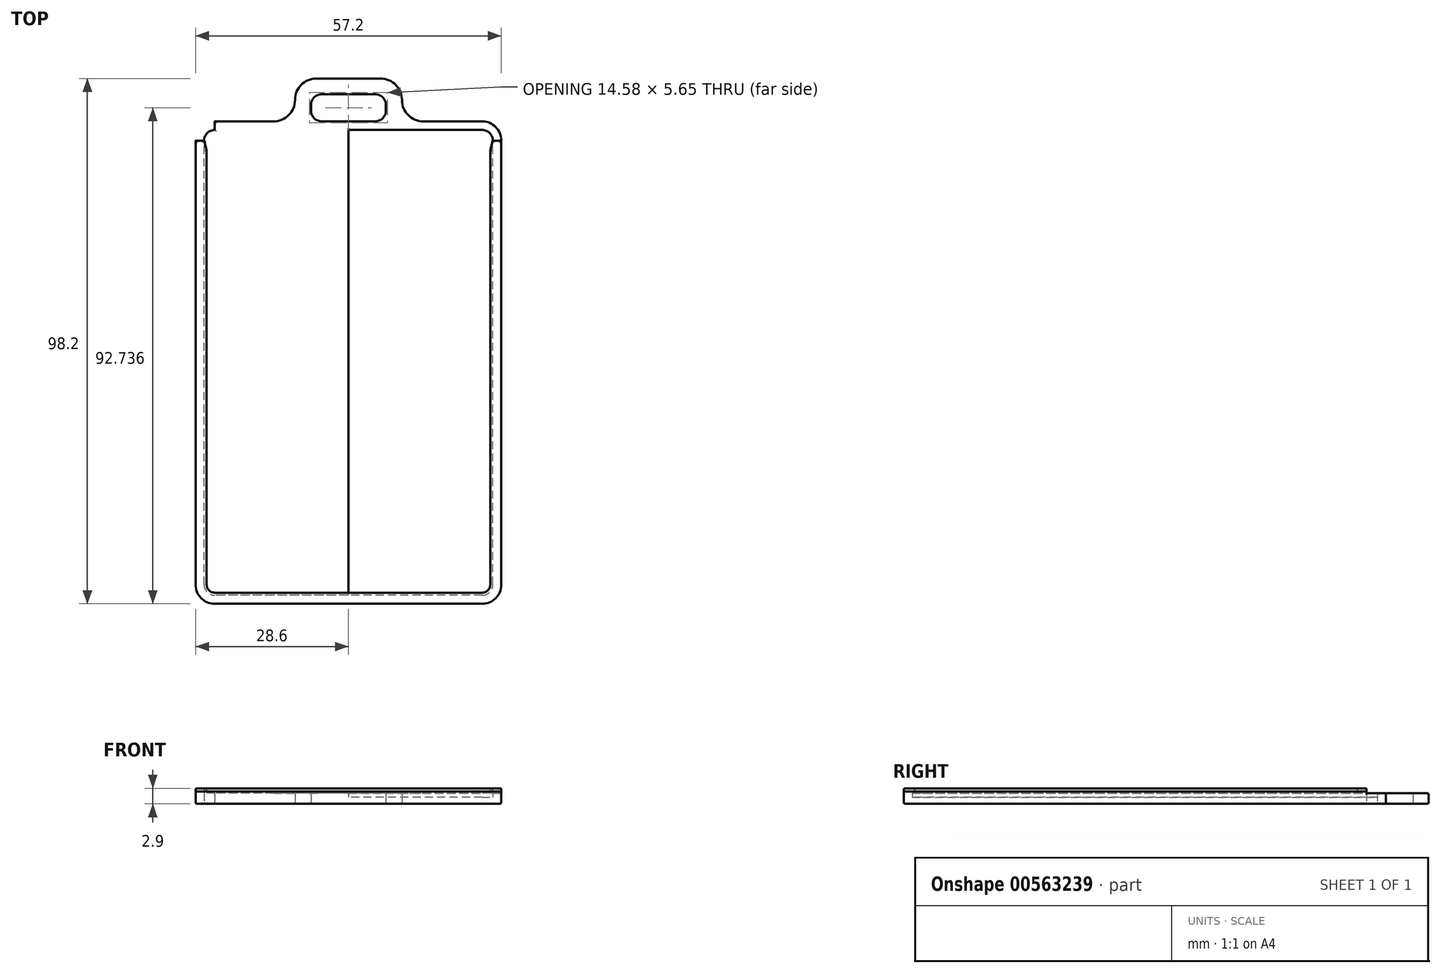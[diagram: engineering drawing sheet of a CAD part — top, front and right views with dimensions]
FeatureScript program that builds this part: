
annotation { "Feature Type Name" : "Feature", "Feature Type Description" : "" }
export const myFeature = defineFeature(function(context is Context, id is Id, definition is map)
    precondition{}
    {
        {
            var Q0;
            Q0=qCreatedBy(makeId("Top.planeOp"),FACE);
            var sketch = newSketch(context, id + "F0", { "sketchPlane" : qUnion([Q0])});
            skLineSegment(sketch, "E0.bottom", {"start": v(0, 0) * mm, "end": v(25, 0) * mm});
            skLineSegment(sketch, "E0.top", {"start": v(0, 87) * mm, "end": v(25, 87) * mm});
            skLineSegment(sketch, "E0.left", {"start": v(0, 0) * mm, "end": v(0, 87) * mm});
            skLineSegment(sketch, "E0.right", {"start": v(27, 2) * mm, "end": v(27, 85) * mm});
            skPoint(sketch, "E1.visualSharp", {"position": v(27, 87) * mm});
            skArc(sketch, "E1.filletArc", {"start": v(27, 85) * mm, "mid": v(26.41, 86.41) * mm, "end": v(25, 87) * mm});
            skPoint(sketch, "E2.visualSharp", {"position": v(27, 0) * mm});
            skArc(sketch, "E2.filletArc", {"start": v(25, 0) * mm, "mid": v(26.41, 0.59) * mm, "end": v(27, 2) * mm});
            skLineSegment(sketch, "E3.0", {"start": v(0, -1.6) * mm, "end": v(25, -1.6) * mm});
            skLineSegment(sketch, "E3.1", {"start": v(0, 88.6) * mm, "end": v(5, 88.6) * mm});
            skArc(sketch, "E3.2", {"start": v(28.6, 85) * mm, "mid": v(27.55, 87.55) * mm, "end": v(25, 88.6) * mm});
            skLineSegment(sketch, "E3.3", {"start": v(28.6, 2) * mm, "end": v(28.6, 85) * mm});
            skArc(sketch, "E3.4", {"start": v(25, -1.6) * mm, "mid": v(27.55, -0.55) * mm, "end": v(28.6, 2) * mm});
            skLineSegment(sketch, "E4", {"start": v(0, 88.6) * mm, "end": v(0, 87) * mm});
            skLineSegment(sketch, "E5", {"start": v(25, 88.6) * mm, "end": v(25, 87) * mm});
            skLineSegment(sketch, "E6", {"start": v(0, -1.6) * mm, "end": v(0, 0) * mm});
            skLineSegment(sketch, "E7", {"start": v(25, 0) * mm, "end": v(25, -1.6) * mm});
            skLineSegment(sketch, "E8", {"start": v(10, 92.6) * mm, "end": v(10, 92.6) * mm});
            skLineSegment(sketch, "E9", {"start": v(6, 96.6) * mm, "end": v(0, 96.6) * mm});
            skLineSegment(sketch, "E10", {"start": v(7, 90.6) * mm, "end": v(7, 91.67) * mm});
            skLineSegment(sketch, "E11", {"start": v(5, 93.67) * mm, "end": v(0, 93.67) * mm});
            skLineSegment(sketch, "E12", {"start": v(0, 93.67) * mm, "end": v(0, 96.6) * mm});
            skPoint(sketch, "E13.visualSharp", {"position": v(7, 93.67) * mm});
            skArc(sketch, "E13.filletArc", {"start": v(7, 91.67) * mm, "mid": v(6.41, 93.09) * mm, "end": v(5, 93.67) * mm});
            skPoint(sketch, "E14.visualSharp", {"position": v(10, 96.6) * mm});
            skArc(sketch, "E14.filletArc", {"start": v(10, 92.6) * mm, "mid": v(8.83, 95.43) * mm, "end": v(6, 96.6) * mm});
            skPoint(sketch, "E15.newPointB", {"position": v(7, 88.67) * mm});
            skArc(sketch, "E15.filletArc", {"start": v(5, 88.6) * mm, "mid": v(6.41, 89.19) * mm, "end": v(7, 90.6) * mm});
            skLineSegment(sketch, "E16", {"start": v(14, 88.6) * mm, "end": v(25, 88.6) * mm});
            skPoint(sketch, "E17.visualSharp", {"position": v(10, 88.6) * mm});
            skArc(sketch, "E17.filletArc", {"start": v(10, 92.6) * mm, "mid": v(11.17, 89.77) * mm, "end": v(14, 88.6) * mm});
            skLineSegment(sketch, "E18", {"start": v(0, 105.46) * mm, "end": v(0, -5) * mm, "construction": true});
            skLineSegment(sketch, "E19.MirrorCS", {"start": v(-6, 96.6) * mm, "end": v(0, 96.6) * mm});
            skLineSegment(sketch, "E20.MirrorCS", {"start": v(-5, 93.67) * mm, "end": v(0, 93.67) * mm});
            skArc(sketch, "E21.MirrorCS", {"start": v(-7, 91.67) * mm, "mid": v(-6.41, 93.09) * mm, "end": v(-5, 93.67) * mm});
            skLineSegment(sketch, "E22.MirrorCS", {"start": v(-7, 90.6) * mm, "end": v(-7, 91.67) * mm});
            skArc(sketch, "E23.MirrorCS", {"start": v(-5, 88.6) * mm, "mid": v(-6.41, 89.19) * mm, "end": v(-7, 90.6) * mm});
            skLineSegment(sketch, "E24.MirrorCS", {"start": v(0, 88.6) * mm, "end": v(-5, 88.6) * mm});
            skArc(sketch, "E25.MirrorCS", {"start": v(-10, 92.6) * mm, "mid": v(-8.83, 95.43) * mm, "end": v(-6, 96.6) * mm});
            skArc(sketch, "E26.MirrorCS", {"start": v(-10, 92.6) * mm, "mid": v(-11.17, 89.77) * mm, "end": v(-14, 88.6) * mm});
            skLineSegment(sketch, "E27.MirrorCS", {"start": v(0, 87) * mm, "end": v(-25, 87) * mm});
            skLineSegment(sketch, "E28.MirrorCS", {"start": v(-14, 88.6) * mm, "end": v(-25, 88.6) * mm});
            skArc(sketch, "E29.MirrorCS", {"start": v(-27, 85) * mm, "mid": v(-26.41, 86.41) * mm, "end": v(-25, 87) * mm});
            skArc(sketch, "E30.MirrorCS", {"start": v(-28.6, 85) * mm, "mid": v(-27.55, 87.55) * mm, "end": v(-25, 88.6) * mm});
            skLineSegment(sketch, "E31.MirrorCS", {"start": v(-28.6, 2) * mm, "end": v(-28.6, 85) * mm});
            skLineSegment(sketch, "E32.MirrorCS", {"start": v(-27, 2) * mm, "end": v(-27, 85) * mm});
            skArc(sketch, "E33.MirrorCS", {"start": v(-25, 0) * mm, "mid": v(-26.41, 0.59) * mm, "end": v(-27, 2) * mm});
            skArc(sketch, "E34.MirrorCS", {"start": v(-25, -1.6) * mm, "mid": v(-27.55, -0.55) * mm, "end": v(-28.6, 2) * mm});
            skLineSegment(sketch, "E35.MirrorCS", {"start": v(-25, 0) * mm, "end": v(-25, -1.6) * mm});
            skLineSegment(sketch, "E36.MirrorCS", {"start": v(0, 0) * mm, "end": v(-25, 0) * mm});
            skLineSegment(sketch, "E37.MirrorCS", {"start": v(0, -1.6) * mm, "end": v(-25, -1.6) * mm});
            skLineSegment(sketch, "E38.MirrorCS", {"start": v(-25, 88.6) * mm, "end": v(-25, 87) * mm});
            skLineSegment(sketch, "E39", {"start": v(-28.6, 85) * mm, "end": v(-27, 85) * mm});
            skLineSegment(sketch, "E40", {"start": v(27, 85) * mm, "end": v(28.6, 85) * mm});
            skPoint(sketch, "E41", {"position": v(0, 50.23) * mm});
            skSolve(sketch);
        }
        {
            var Q0;
            Q0=makeQuery(id+"F0.imprint","IMPRINT",FACE,{"disambiguationData":[TD([[makeQuery(id+"F0.imprint","IMPRINT",EDGE,{"derivedFrom":sQuery(id+"F0.wireOp",EDGE,"E0.left")}),1.0]])]});
            var Q1;
            Q1=makeQuery(id+"F0.imprint","IMPRINT",FACE,{"disambiguationData":[TD([[makeQuery(id+"F0.imprint","IMPRINT",EDGE,{"derivedFrom":sQuery(id+"F0.wireOp",EDGE,"E0.bottom")}),1.0]])]});
            extrude(context, id + "F1", {"entities" : qUnion([Q0, Q1]), "depth" : 1.2 * mm, "offsetDistance" : 25 * mm});
        }
        {
            var Q0;
            Q0=makeQuery(id+"F0.imprint","IMPRINT",FACE,{"disambiguationData":[TD([[makeQuery(id+"F0.imprint","IMPRINT",EDGE,{"derivedFrom":sQuery(id+"F0.wireOp",EDGE,"E0.right")}),-1.0]])]});
            var Q1;
            Q1=makeQuery(id+"F0.imprint","IMPRINT",FACE,{"disambiguationData":[TD([[makeQuery(id+"F0.imprint","IMPRINT",EDGE,{"derivedFrom":sQuery(id+"F0.wireOp",EDGE,"E6")}),1.0]])]});
            var Q2;
            Q2=makeQuery(id+"F0.imprint","IMPRINT",FACE,{"disambiguationData":[TD([[makeQuery(id+"F0.imprint","IMPRINT",EDGE,{"derivedFrom":sQuery(id+"F0.wireOp",EDGE,"E0.bottom")}),-1.0]])]});
            var Q3;
            Q3=makeQuery(id+"F0.imprint","IMPRINT",FACE,{"disambiguationData":[TD([[makeQuery(id+"F0.imprint","IMPRINT",EDGE,{"derivedFrom":sQuery(id+"F0.wireOp",EDGE,"E31.MirrorCS")}),-1.0]])]});
            extrude(context, id + "F2", {"entities" : qUnion([Q0, Q1, Q2, Q3]), "operationType" : NewBodyOperationType.ADD, "depth" : 2.3 * mm, "offsetDistance" : 25 * mm});
        }
        {
            var Q0;
            Q0=makeQuery(id+"F2.opExtrude","CAP_FACE",FACE,{"disambiguationData":[OSD([sQuery(id+"F0.wireOp",EDGE,"E0.bottom"),sQuery(id+"F0.wireOp",EDGE,"E0.top"),sQuery(id+"F0.wireOp",EDGE,"E0.right"),sQuery(id+"F0.wireOp",EDGE,"E1.filletArc"),sQuery(id+"F0.wireOp",EDGE,"E2.filletArc"),sQuery(id+"F0.wireOp",EDGE,"E3.0"),sQuery(id+"F0.wireOp",EDGE,"E3.1"),sQuery(id+"F0.wireOp",EDGE,"E3.2"),sQuery(id+"F0.wireOp",EDGE,"E3.3"),sQuery(id+"F0.wireOp",EDGE,"E3.4"),sQuery(id+"F0.wireOp",EDGE,"E9"),sQuery(id+"F0.wireOp",EDGE,"E10"),sQuery(id+"F0.wireOp",EDGE,"E11"),sQuery(id+"F0.wireOp",EDGE,"E13.filletArc"),sQuery(id+"F0.wireOp",EDGE,"E14.filletArc"),sQuery(id+"F0.wireOp",EDGE,"E15.filletArc"),sQuery(id+"F0.wireOp",EDGE,"E16"),sQuery(id+"F0.wireOp",EDGE,"E17.filletArc"),sQuery(id+"F0.wireOp",EDGE,"E19.MirrorCS"),sQuery(id+"F0.wireOp",EDGE,"E20.MirrorCS"),sQuery(id+"F0.wireOp",EDGE,"E21.MirrorCS"),sQuery(id+"F0.wireOp",EDGE,"E22.MirrorCS"),sQuery(id+"F0.wireOp",EDGE,"E23.MirrorCS"),sQuery(id+"F0.wireOp",EDGE,"E24.MirrorCS"),sQuery(id+"F0.wireOp",EDGE,"E25.MirrorCS"),sQuery(id+"F0.wireOp",EDGE,"E26.MirrorCS"),sQuery(id+"F0.wireOp",EDGE,"E27.MirrorCS"),sQuery(id+"F0.wireOp",EDGE,"E28.MirrorCS"),sQuery(id+"F0.wireOp",EDGE,"E29.MirrorCS"),sQuery(id+"F0.wireOp",EDGE,"E30.MirrorCS"),sQuery(id+"F0.wireOp",EDGE,"E31.MirrorCS"),sQuery(id+"F0.wireOp",EDGE,"E32.MirrorCS"),sQuery(id+"F0.wireOp",EDGE,"E33.MirrorCS"),sQuery(id+"F0.wireOp",EDGE,"E34.MirrorCS"),sQuery(id+"F0.wireOp",EDGE,"E36.MirrorCS"),sQuery(id+"F0.wireOp",EDGE,"E37.MirrorCS")])],"isStart":false});
            var sketch = newSketch(context, id + "F3", { "sketchPlane" : qUnion([Q0])});
            skArc(sketch, "E42.0", {"start": v(-26.52, 2) * mm, "mid": v(-26.07, 0.93) * mm, "end": v(-25, 0.48) * mm});
            skLineSegment(sketch, "E42.1", {"start": v(-26.52, 85) * mm, "end": v(-26.52, 2) * mm});
            skLineSegment(sketch, "E42.2", {"start": v(-25, 0.48) * mm, "end": v(25, 0.48) * mm});
            skArc(sketch, "E42.3", {"start": v(-25, 86.52) * mm, "mid": v(-26.07, 86.07) * mm, "end": v(-26.52, 85) * mm});
            skArc(sketch, "E42.4", {"start": v(25, 0.48) * mm, "mid": v(26.07, 0.93) * mm, "end": v(26.52, 2) * mm});
            skLineSegment(sketch, "E42.5", {"start": v(26.52, 2) * mm, "end": v(26.52, 85) * mm});
            skArc(sketch, "E42.6", {"start": v(26.52, 85) * mm, "mid": v(26.07, 86.07) * mm, "end": v(25, 86.52) * mm});
            skLineSegment(sketch, "E42.7", {"start": v(25, 86.52) * mm, "end": v(-25, 86.52) * mm});
            skLineSegment(sketch, "E43", {"start": v(-26.52, 85) * mm, "end": v(-28.6, 85) * mm});
            skLineSegment(sketch, "E44", {"start": v(26.52, 85) * mm, "end": v(28.6, 85) * mm});
            skLineSegment(sketch, "E45", {"start": v(27, 85) * mm, "end": v(26.52, 83.24) * mm});
            skLineSegment(sketch, "E46", {"start": v(-27, 85) * mm, "end": v(-26.52, 83.24) * mm});
            skSolve(sketch);
        }
        {
            var Q0;
            Q0=makeQuery(id+"F3.imprint","IMPRINT",FACE,{"disambiguationData":[TD([[makeQuery(id+"F3.imprint","IMPRINT",EDGE,{"derivedFrom":sQuery(id+"F3.wireOp",EDGE,"E42.0")}),-1.0]])]});
            var Q1;
            Q1=makeQuery(id+"F3.imprint","IMPRINT",FACE,{"disambiguationData":[TD([[makeQuery(id+"F3.imprint","IMPRINT",EDGE,{"derivedFrom":makeQuery(id+"F2.opExtrude","CAP_EDGE",EDGE,{"disambiguationData":[OSD([sQuery(id+"F0.wireOp",EDGE,"E0.right")])],"isStart":false})}),-1.0]])]});
            extrude(context, id + "F4", {"entities" : qUnion([Q0, Q1]), "depth" : 0.6 * mm, "offsetDistance" : 25 * mm});
        }
        {
            var Q0;
            Q0=makeQuery(id+"F4.opExtrude","CAP_EDGE",EDGE,{"disambiguationData":[OSD([sQuery(id+"F0.wireOp",EDGE,"E31.MirrorCS")])],"isStart":false});
            var Q1;
            Q1=makeQuery(id+"F4.opExtrude","CAP_EDGE",EDGE,{"disambiguationData":[OSD([sQuery(id+"F3.wireOp",EDGE,"E43")])],"isStart":false});
            var Q2;
            Q2=makeQuery(id+"F4.opExtrude","CAP_EDGE",EDGE,{"disambiguationData":[OSD([sQuery(id+"F3.wireOp",EDGE,"E46")])],"isStart":false});
            var Q3;
            Q3=makeQuery(id+"F4.opExtrude","CAP_EDGE",EDGE,{"disambiguationData":[OSD([sQuery(id+"F3.wireOp",EDGE,"E42.1")])],"isStart":false});
            var Q4;
            Q4=makeQuery(id+"F4.opExtrude","CAP_EDGE",EDGE,{"disambiguationData":[OSD([sQuery(id+"F3.wireOp",EDGE,"E45")])],"isStart":false});
            var Q5;
            Q5=makeQuery(id+"F4.opExtrude","CAP_EDGE",EDGE,{"disambiguationData":[OSD([sQuery(id+"F3.wireOp",EDGE,"E44")])],"isStart":false});
            var Q6;
            Q6=makeQuery(id+"F4.opExtrude","CAP_EDGE",EDGE,{"disambiguationData":[OSD([sQuery(id+"F3.wireOp",EDGE,"E42.5")])],"isStart":true});
            var Q7;
            Q7=makeQuery(id+"F4.opExtrude","CAP_EDGE",EDGE,{"disambiguationData":[OSD([sQuery(id+"F3.wireOp",EDGE,"E45")])],"isStart":true});
            var Q8;
            Q8=makeQuery(id+"F4.opExtrude","CAP_EDGE",EDGE,{"disambiguationData":[OSD([sQuery(id+"F3.wireOp",EDGE,"E46")])],"isStart":true});
            fillet(context, id + "F5", {"entities" : qUnion([Q0, Q1, Q2, Q3, Q4, Q5, Q6, Q7, Q8]), "radius" : 0.27 * mm, "tangentPropagation" : true, "allowEdgeOverflow" : false});
        }
        {
            var Q0;
            Q0=makeQuery(id+"F0.imprint","IMPRINT",FACE,{"disambiguationData":[TD([[makeQuery(id+"F0.imprint","IMPRINT",EDGE,{"derivedFrom":sQuery(id+"F0.wireOp",EDGE,"E0.top")}),1.0]])]});
            var Q1;
            Q1=makeQuery(id+"F0.imprint","IMPRINT",FACE,{"disambiguationData":[TD([[makeQuery(id+"F0.imprint","IMPRINT",EDGE,{"derivedFrom":sQuery(id+"F0.wireOp",EDGE,"E1.filletArc")}),-1.0]])]});
            var Q2;
            Q2=makeQuery(id+"F0.imprint","IMPRINT",FACE,{"disambiguationData":[TD([[makeQuery(id+"F0.imprint","IMPRINT",EDGE,{"derivedFrom":sQuery(id+"F0.wireOp",EDGE,"E4")}),-1.0]])]});
            var Q3;
            Q3=makeQuery(id+"F0.imprint","IMPRINT",FACE,{"disambiguationData":[TD([[makeQuery(id+"F0.imprint","IMPRINT",EDGE,{"derivedFrom":sQuery(id+"F0.wireOp",EDGE,"E29.MirrorCS")}),1.0]])]});
            var Q4;
            Q4=sQuery(id+"F0.wireOp",EDGE,"E14.filletArc");
            var Q5;
            Q5=sQuery(id+"F0.wireOp",EDGE,"E9");
            var Q6;
            Q6=sQuery(id+"F0.wireOp",EDGE,"E17.filletArc");
            var Q7;
            Q7=sQuery(id+"F0.wireOp",EDGE,"E16");
            var Q8;
            Q8=sQuery(id+"F0.wireOp",EDGE,"E5");
            var Q9;
            Q9=sQuery(id+"F0.wireOp",EDGE,"E0.top");
            var Q10;
            Q10=sQuery(id+"F0.wireOp",EDGE,"E4");
            var Q11;
            Q11=sQuery(id+"F0.wireOp",EDGE,"E3.1");
            var Q12;
            Q12=sQuery(id+"F0.wireOp",EDGE,"E15.filletArc");
            var Q13;
            Q13=sQuery(id+"F0.wireOp",EDGE,"E13.filletArc");
            var Q14;
            Q14=sQuery(id+"F0.wireOp",EDGE,"E11");
            var Q15;
            Q15=sQuery(id+"F0.wireOp",EDGE,"E12");
            extrude(context, id + "F6", {"entities" : qUnion([Q0, Q1, Q2, Q3]), "operationType" : NewBodyOperationType.ADD, "surfaceEntities" : qUnion([Q4, Q5, Q6, Q7, Q8, Q9, Q10, Q11, Q12, Q13, Q14, Q15]), "depth" : 2 * mm, "offsetDistance" : 25 * mm});
        }
        {
            var Q0;
            Q0=makeQuery(id+"F6.opExtrude","CAP_EDGE",EDGE,{"disambiguationData":[OSD([sQuery(id+"F0.wireOp",EDGE,"E28.MirrorCS")])],"isStart":false});
            var Q1;
            Q1=makeQuery(id+"F6.opExtrude","CAP_EDGE",EDGE,{"disambiguationData":[OSD([sQuery(id+"F0.wireOp",EDGE,"E23.MirrorCS")])],"isStart":false});
            var Q2;
            Q2=makeQuery(id+"F6.opExtrude","CAP_EDGE",EDGE,{"disambiguationData":[OSD([sQuery(id+"F0.wireOp",EDGE,"E11"),sQuery(id+"F0.wireOp",EDGE,"E20.MirrorCS")])],"isStart":true});
            var Q3;
            Q3=makeQuery(id+"F6.opExtrude","CAP_EDGE",EDGE,{"disambiguationData":[OSD([sQuery(id+"F0.wireOp",EDGE,"E0.top"),sQuery(id+"F0.wireOp",EDGE,"E27.MirrorCS")])],"isStart":false});
            var Q4;
            Q4=makeQuery(id+"F2.opExtrude","CAP_EDGE",EDGE,{"disambiguationData":[OSD([sQuery(id+"F0.wireOp",EDGE,"E3.3")])],"isStart":true});
            var Q5;
            Q5=makeQuery(id+"F1.opExtrude","CAP_EDGE",EDGE,{"disambiguationData":[OSD([sQuery(id+"F0.wireOp",EDGE,"9OIkUDAE-OhTw-2ISP-A8b7-w3id6OZFLPig")])],"isStart":false});
            var Q6;
            Q6=makeQuery(id+"F1.opExtrude","CAP_EDGE",EDGE,{"disambiguationData":[OSD([sQuery(id+"F0.wireOp",EDGE,"w27zVd3O-8vEv-FC9z-3hRh-1JZhNeqeYrMk")])],"isStart":false});
            var Q7;
            Q7=makeQuery(id+"F1.opExtrude","CAP_EDGE",EDGE,{"disambiguationData":[OSD([sQuery(id+"F0.wireOp",EDGE,"bKtwGkjI-SjTx-TJVN-z7t7-ZLo4pZOKJZ8O")])],"isStart":false});
            var Q8;
            Q8=makeQuery(id+"F1.opExtrude","CAP_EDGE",EDGE,{"disambiguationData":[OSD([sQuery(id+"F0.wireOp",EDGE,"MdrqjnWr-6qWE-170S-hCw8-gow3h5K4mK9a")])],"isStart":false});
            var Q9;
            Q9=makeQuery(id+"F1.opExtrude","CAP_EDGE",EDGE,{"disambiguationData":[OSD([sQuery(id+"F0.wireOp",EDGE,"ZVlLO4as-SFDz-RjLi-tBlu-AObxJnyWLo8c")])],"isStart":false});
            var Q10;
            Q10=makeQuery(id+"F1.opExtrude","CAP_EDGE",EDGE,{"disambiguationData":[OSD([sQuery(id+"F0.wireOp",EDGE,"7zTt4tq9-GIZ7-Z6Lu-evoY-hsrNUiY6z4SB")])],"isStart":false});
            var Q11;
            {var subQ0=sQuery(id+"F0.wireOp",EDGE,"E40");var subQ1=sQuery(id+"F0.wireOp",EDGE,"E39");var subQ2=sQuery(id+"F0.wireOp",EDGE,"E29.MirrorCS");var subQ3=sQuery(id+"F0.wireOp",EDGE,"E27.MirrorCS");var subQ4=sQuery(id+"F0.wireOp",EDGE,"E1.filletArc");var subQ5=sQuery(id+"F0.wireOp",EDGE,"E0.top");var subQ6=sQuery(id+"F0.wireOp",EDGE,"E36.MirrorCS");var subQ7=sQuery(id+"F0.wireOp",EDGE,"E33.MirrorCS");var subQ8=sQuery(id+"F0.wireOp",EDGE,"E32.MirrorCS");var subQ9=sQuery(id+"F0.wireOp",EDGE,"E2.filletArc");var subQ10=sQuery(id+"F0.wireOp",EDGE,"E0.right");var subQ11=sQuery(id+"F0.wireOp",EDGE,"E0.bottom");Q11=makeQuery(id+"F6.boolean.opBoolean","MERGE",FACE,{"derivedFrom":[makeQuery(id+"F2.boolean.opBoolean","MERGE",FACE,{"derivedFrom":[makeQuery(id+"F1.opExtrude","CAP_FACE",FACE,{"disambiguationData":[OSD([subQ11,subQ5,subQ10,subQ4,subQ9,subQ3,subQ2,subQ8,subQ7,subQ6,sQuery(id+"F0.wireOp",EDGE,"1rFzYcFG-Mo6D-CwZs-4op5-U56MTfyKJgBB"),sQuery(id+"F0.wireOp",EDGE,"7zTt4tq9-GIZ7-Z6Lu-evoY-hsrNUiY6z4SB"),sQuery(id+"F0.wireOp",EDGE,"ZVlLO4as-SFDz-RjLi-tBlu-AObxJnyWLo8c"),sQuery(id+"F0.wireOp",EDGE,"MdrqjnWr-6qWE-170S-hCw8-gow3h5K4mK9a"),sQuery(id+"F0.wireOp",EDGE,"w27zVd3O-8vEv-FC9z-3hRh-1JZhNeqeYrMk"),sQuery(id+"F0.wireOp",EDGE,"9OIkUDAE-OhTw-2ISP-A8b7-w3id6OZFLPig"),sQuery(id+"F0.wireOp",EDGE,"bKtwGkjI-SjTx-TJVN-z7t7-ZLo4pZOKJZ8O")])],"isStart":true}),makeQuery(id+"F2.opExtrude","CAP_FACE",FACE,{"disambiguationData":[OSD([subQ11,subQ10,subQ9,sQuery(id+"F0.wireOp",EDGE,"E3.0"),sQuery(id+"F0.wireOp",EDGE,"E3.3"),sQuery(id+"F0.wireOp",EDGE,"E3.4"),sQuery(id+"F0.wireOp",EDGE,"E31.MirrorCS"),subQ8,subQ7,sQuery(id+"F0.wireOp",EDGE,"E34.MirrorCS"),subQ6,sQuery(id+"F0.wireOp",EDGE,"E37.MirrorCS"),subQ1,subQ0])],"isStart":true})]}),makeQuery(id+"F6.opExtrude","CAP_FACE",FACE,{"disambiguationData":[OSD([subQ5,subQ4,sQuery(id+"F0.wireOp",EDGE,"E3.1"),sQuery(id+"F0.wireOp",EDGE,"E3.2"),sQuery(id+"F0.wireOp",EDGE,"E9"),sQuery(id+"F0.wireOp",EDGE,"E10"),sQuery(id+"F0.wireOp",EDGE,"E11"),sQuery(id+"F0.wireOp",EDGE,"E13.filletArc"),sQuery(id+"F0.wireOp",EDGE,"E14.filletArc"),sQuery(id+"F0.wireOp",EDGE,"E15.filletArc"),sQuery(id+"F0.wireOp",EDGE,"E16"),sQuery(id+"F0.wireOp",EDGE,"E17.filletArc"),sQuery(id+"F0.wireOp",EDGE,"E19.MirrorCS"),sQuery(id+"F0.wireOp",EDGE,"E20.MirrorCS"),sQuery(id+"F0.wireOp",EDGE,"E21.MirrorCS"),sQuery(id+"F0.wireOp",EDGE,"E22.MirrorCS"),sQuery(id+"F0.wireOp",EDGE,"E23.MirrorCS"),sQuery(id+"F0.wireOp",EDGE,"E24.MirrorCS"),sQuery(id+"F0.wireOp",EDGE,"E25.MirrorCS"),sQuery(id+"F0.wireOp",EDGE,"E26.MirrorCS"),subQ3,sQuery(id+"F0.wireOp",EDGE,"E28.MirrorCS"),subQ2,sQuery(id+"F0.wireOp",EDGE,"E30.MirrorCS"),subQ1,subQ0])],"isStart":true})]});}
            var Q12;
            Q12=makeQuery(id+"F1.opExtrude","CAP_EDGE",EDGE,{"disambiguationData":[OSD([sQuery(id+"F0.wireOp",EDGE,"YS9L8whu-aNZT-wEhm-iBkx-pPmlFqo6A8m6")])],"isStart":false});
            var Q13;
            Q13=makeQuery(id+"F1.opExtrude","CAP_EDGE",EDGE,{"disambiguationData":[OSD([sQuery(id+"F0.wireOp",EDGE,"23uT0CqP-QJSQ-l8G1-THvL-nSwdamfE2bE5")])],"isStart":false});
            var Q14;
            {var subQ0=sQuery(id+"F0.wireOp",EDGE,"YS9L8whu-aNZT-wEhm-iBkx-pPmlFqo6A8m6");Q14=makeQuery(id+"F2.boolean.opBoolean","MERGE",EDGE,{"derivedFrom":[makeQuery(id+"F1.opExtrude","CAP_EDGE",EDGE,{"disambiguationData":[OSD([subQ0])],"isStart":true}),makeQuery(id+"F2.opExtrude","CAP_EDGE",EDGE,{"disambiguationData":[OSD([subQ0])],"isStart":true})]});}
            var Q15;
            Q15=makeQuery(id+"F1.opExtrude","CAP_EDGE",EDGE,{"disambiguationData":[OSD([sQuery(id+"F0.wireOp",EDGE,"23uT0CqP-QJSQ-l8G1-THvL-nSwdamfE2bE5")])],"isStart":true});
            fillet(context, id + "F7", {"entities" : qUnion([Q0, Q1, Q2, Q3, Q4, Q5, Q6, Q7, Q8, Q9, Q10, Q11, Q12, Q13, Q14, Q15]), "radius" : 0.29 * mm, "tangentPropagation" : true, "allowEdgeOverflow" : false});
        }
    });
